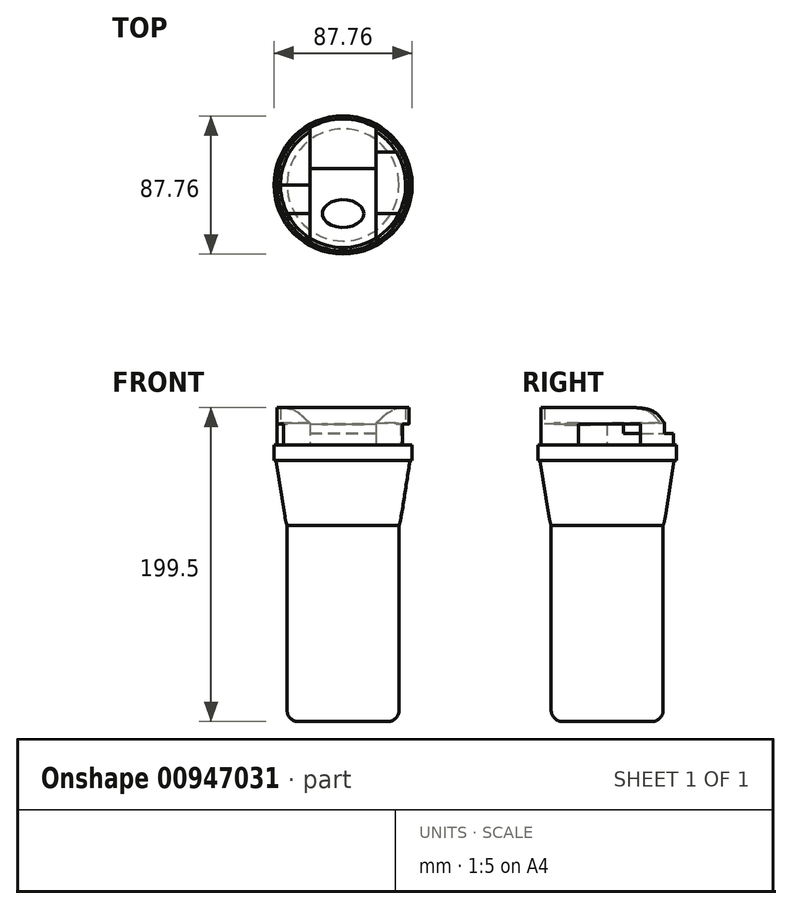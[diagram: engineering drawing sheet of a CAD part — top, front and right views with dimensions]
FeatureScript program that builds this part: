
annotation { "Feature Type Name" : "Feature", "Feature Type Description" : "" }
export const myFeature = defineFeature(function(context is Context, id is Id, definition is map)
    precondition{}
    {
        {
            var Q0;
            Q0=qCreatedBy(makeId("Top.planeOp"),FACE);
            var sketch = newSketch(context, id + "F0", { "sketchPlane" : qUnion([Q0])});
            skCircle(sketch, "E0", {"center": v(0, 0) * mm, "radius": 35.56 * mm});
            skSolve(sketch);
        }
        {
            var Q0;
            Q0 = qSketchRegion(id + "F0", true);
            extrude(context, id + "F1", {"entities" : qUnion([Q0]), "depth" : 124.6 * mm, "offsetDistance" : 25 * mm});
        }
        {
            var Q0;
            Q0=makeQuery(id+"F1.opExtrude","CAP_FACE",FACE,{"disambiguationData":[OSD([sQuery(id+"F0.wireOp",EDGE,"E0")])],"isStart":false});
            var sketch = newSketch(context, id + "F2", { "sketchPlane" : qUnion([Q0])});
            skCircle(sketch, "E1", {"center": v(0, 0) * mm, "radius": 36.06 * mm});
            skSolve(sketch);
        }
        {
            var Q0;
            Q0 = qSketchRegion(id + "F2", true);
            extrude(context, id + "F3", {"entities" : qUnion([Q0]), "operationType" : NewBodyOperationType.ADD, "depth" : 41.22 * mm, "offsetDistance" : 25 * mm});
        }
        {
            var Q0;
            Q0=makeQuery(id+"F3.opExtrude","CAP_FACE",FACE,{"disambiguationData":[OSD([sQuery(id+"F2.wireOp",EDGE,"E1")])],"isStart":false});
            var sketch = newSketch(context, id + "F4", { "sketchPlane" : qUnion([Q0])});
            skCircle(sketch, "E2", {"center": v(0, 0) * mm, "radius": 42.57 * mm});
            skSolve(sketch);
        }
        {
            var Q0;
            Q0 = qSketchRegion(id + "F4", true);
            extrude(context, id + "F5", {"entities" : qUnion([Q0]), "operationType" : NewBodyOperationType.ADD, "depth" : 0.1 * mm, "offsetDistance" : 25 * mm});
        }
        {
            var Q1;
            Q1 = qSketchRegion(id + "F4", true);
            var Q2;
            Q2 = qSketchRegion(id + "F2", true);
            loft(context, id + "F6", {"operationType" : NewBodyOperationType.ADD, "sheetProfilesArray" : [{ "sheetProfileEntities" : qUnion([Q1]) }, { "sheetProfileEntities" : qUnion([Q2]) }]});
        }
        {
            var Q0;
            Q0=makeQuery(id+"F5.opExtrude","CAP_FACE",FACE,{"disambiguationData":[OSD([sQuery(id+"F4.wireOp",EDGE,"E2")])],"isStart":false});
            var sketch = newSketch(context, id + "F7", { "sketchPlane" : qUnion([Q0])});
            skCircle(sketch, "E3", {"center": v(0, 0) * mm, "radius": 43.88 * mm});
            skSolve(sketch);
        }
        {
            var Q0;
            Q0 = qSketchRegion(id + "F7", true);
            extrude(context, id + "F8", {"entities" : qUnion([Q0]), "operationType" : NewBodyOperationType.ADD, "depth" : 9.9 * mm, "offsetDistance" : 25 * mm});
        }
        {
            var Q0;
            Q0=makeQuery(id+"F8.opExtrude","CAP_FACE",FACE,{"disambiguationData":[OSD([sQuery(id+"F7.wireOp",EDGE,"E3")])],"isStart":false});
            var sketch = newSketch(context, id + "F9", { "sketchPlane" : qUnion([Q0])});
            skCircle(sketch, "E4", {"center": v(0, 0) * mm, "radius": 41.98 * mm});
            skLineSegment(sketch, "E5", {"start": v(-41.98, 0) * mm, "end": v(41.98, 0) * mm});
            skLineSegment(sketch, "E6", {"start": v(0, 43.88) * mm, "end": v(0, -43.88) * mm});
            skLineSegment(sketch, "E7", {"start": v(0, 0) * mm, "end": v(41.98, 0) * mm});
            skLineSegment(sketch, "E8", {"start": v(0, 0) * mm, "end": v(-41.98, 0) * mm});
            skLineSegment(sketch, "E9", {"start": v(-20.99, 0) * mm, "end": v(-20.99, 36.35) * mm});
            skLineSegment(sketch, "E10", {"start": v(-20.99, 0) * mm, "end": v(-20.99, -36.35) * mm});
            skLineSegment(sketch, "E11", {"start": v(20.99, 0) * mm, "end": v(20.99, 36.35) * mm});
            skLineSegment(sketch, "E12", {"start": v(20.99, 0) * mm, "end": v(20.99, -36.35) * mm});
            skLineSegment(sketch, "E13", {"start": v(0, 0) * mm, "end": v(0, -41.98) * mm});
            skLineSegment(sketch, "E14", {"start": v(0, 0) * mm, "end": v(0, 41.98) * mm});
            skLineSegment(sketch, "E15", {"start": v(0, 20.99) * mm, "end": v(-36.35, 20.99) * mm});
            skLineSegment(sketch, "E16", {"start": v(0, 20.99) * mm, "end": v(36.35, 20.99) * mm});
            skLineSegment(sketch, "E17", {"start": v(-37.84, -18.18) * mm, "end": v(0, -18.18) * mm});
            skPoint(sketch, "E17.startSnap0", {"position": v(-20.99, -18.18) * mm});
            skLineSegment(sketch, "E18", {"start": v(0, -18.18) * mm, "end": v(37.84, -18.18) * mm});
            skLineSegment(sketch, "E19", {"start": v(-20.99, 20.99) * mm, "end": v(-20.99, 0) * mm});
            skLineSegment(sketch, "E20", {"start": v(-20.99, 10.5) * mm, "end": v(20.99, 10.5) * mm});
            skEllipse(sketch, "E21", {"center": v(0, -18.18) * mm, "majorRadius": 13.21 * mm, "minorRadius": 8.8 * mm, "majorAxis": v(1, 0)});
            skSolve(sketch);
        }
        {
            var Q0;
            {var subQ0=sQuery(id+"F9.wireOp",EDGE,"E11");var subQ1=sQuery(id+"F9.wireOp",EDGE,"E4");var subQ2=makeQuery(id+"F9.imprint","INTERSECT",VERTEX,{"derivedFrom":[subQ1,subQ0]});Q0=makeQuery(id+"F9.imprint","IMPRINT",FACE,{"disambiguationData":[TD([[makeQuery(id+"F9.imprint","IMPRINT",EDGE,{"disambiguationData":[TD([[subQ2,1.0]])],"derivedFrom":subQ0}),1.0]])]});}
            var Q1;
            {var subQ0=sQuery(id+"F9.wireOp",EDGE,"E9");Q1=makeQuery(id+"F9.imprint","IMPRINT",FACE,{"disambiguationData":[TD([[makeQuery(id+"F9.imprint","IMPRINT",EDGE,{"derivedFrom":subQ0}),-1.0]])]});}
            var Q2;
            {var subQ3=sQuery(id+"F9.wireOp",EDGE,"E20");var subQ5=sQuery(id+"F9.wireOp",EDGE,"E19");var subQ7=makeQuery(id+"F9.imprint","INTERSECT",VERTEX,{"derivedFrom":[subQ5,subQ3]});Q2=makeQuery(id+"F9.imprint","IMPRINT",FACE,{"disambiguationData":[TD([[makeQuery(id+"F9.imprint","IMPRINT",EDGE,{"disambiguationData":[TD([[subQ7,-1.0]])],"derivedFrom":subQ3}),1.0]])]});}
            var Q3;
            {var subQ0=sQuery(id+"F9.wireOp",EDGE,"E20");var subQ1=sQuery(id+"F9.wireOp",EDGE,"E11");var subQ2=makeQuery(id+"F9.imprint","INTERSECT",VERTEX,{"derivedFrom":[subQ1,subQ0]});Q3=makeQuery(id+"F9.imprint","IMPRINT",FACE,{"disambiguationData":[TD([[makeQuery(id+"F9.imprint","IMPRINT",EDGE,{"disambiguationData":[TD([[subQ2,-1.0]])],"derivedFrom":subQ1}),1.0]])]});}
            extrude(context, id + "F10", {"entities" : qUnion([Q0, Q1, Q2, Q3]), "operationType" : NewBodyOperationType.ADD, "flatOperationType" : FlatOperationType.REMOVE, "depth" : 7.1 * mm, "offsetDistance" : 25 * mm, "domain" : OperationDomain.MODEL});
        }
        {
            var Q0;
            {var subQ0=sQuery(id+"F9.wireOp",EDGE,"E9");Q0=makeQuery(id+"F9.imprint","IMPRINT",FACE,{"disambiguationData":[TD([[makeQuery(id+"F9.imprint","IMPRINT",EDGE,{"derivedFrom":subQ0}),1.0]])]});}
            var Q1;
            {var subQ4=sQuery(id+"F9.wireOp",EDGE,"E8");var subQ5=sQuery(id+"F9.wireOp",EDGE,"E4");var subQ6=makeQuery(id+"F9.imprint","INTERSECT",VERTEX,{"derivedFrom":[subQ5,subQ4]});Q1=makeQuery(id+"F9.imprint","IMPRINT",FACE,{"disambiguationData":[TD([[makeQuery(id+"F9.imprint","IMPRINT",EDGE,{"disambiguationData":[TD([[subQ6,1.0]])],"derivedFrom":subQ5}),1.0]])]});}
            var Q2;
            {var subQ0=sQuery(id+"F9.wireOp",EDGE,"E8");var subQ1=sQuery(id+"F9.wireOp",EDGE,"E4");var subQ2=makeQuery(id+"F9.imprint","INTERSECT",VERTEX,{"derivedFrom":[subQ1,subQ0]});Q2=makeQuery(id+"F9.imprint","IMPRINT",FACE,{"disambiguationData":[TD([[makeQuery(id+"F9.imprint","IMPRINT",EDGE,{"disambiguationData":[TD([[subQ2,-1.0]])],"derivedFrom":subQ1}),1.0]])]});}
            var Q3;
            {var subQ0=sQuery(id+"F9.wireOp",EDGE,"E10");var subQ1=sQuery(id+"F9.wireOp",EDGE,"E4");var subQ2=makeQuery(id+"F9.imprint","INTERSECT",VERTEX,{"derivedFrom":[subQ1,subQ0]});Q3=makeQuery(id+"F9.imprint","IMPRINT",FACE,{"disambiguationData":[TD([[makeQuery(id+"F9.imprint","IMPRINT",EDGE,{"disambiguationData":[TD([[subQ2,1.0]])],"derivedFrom":subQ1}),1.0]])]});}
            var Q4;
            {var subQ0=sQuery(id+"F9.wireOp",EDGE,"E11");var subQ1=sQuery(id+"F9.wireOp",EDGE,"E4");var subQ2=makeQuery(id+"F9.imprint","INTERSECT",VERTEX,{"derivedFrom":[subQ1,subQ0]});Q4=makeQuery(id+"F9.imprint","IMPRINT",FACE,{"disambiguationData":[TD([[makeQuery(id+"F9.imprint","IMPRINT",EDGE,{"disambiguationData":[TD([[subQ2,1.0]])],"derivedFrom":subQ1}),1.0]])]});}
            var Q5;
            {var subQ4=sQuery(id+"F9.wireOp",EDGE,"E7");var subQ5=sQuery(id+"F9.wireOp",EDGE,"E4");var subQ6=makeQuery(id+"F9.imprint","INTERSECT",VERTEX,{"derivedFrom":[subQ5,subQ4]});Q5=makeQuery(id+"F9.imprint","IMPRINT",FACE,{"disambiguationData":[TD([[makeQuery(id+"F9.imprint","IMPRINT",EDGE,{"disambiguationData":[TD([[subQ6,-1.0]])],"derivedFrom":subQ5}),1.0]])]});}
            var Q6;
            {var subQ0=sQuery(id+"F9.wireOp",EDGE,"E7");var subQ1=sQuery(id+"F9.wireOp",EDGE,"E4");var subQ2=makeQuery(id+"F9.imprint","INTERSECT",VERTEX,{"derivedFrom":[subQ1,subQ0]});Q6=makeQuery(id+"F9.imprint","IMPRINT",FACE,{"disambiguationData":[TD([[makeQuery(id+"F9.imprint","IMPRINT",EDGE,{"disambiguationData":[TD([[subQ2,1.0]])],"derivedFrom":subQ1}),1.0]])]});}
            var Q7;
            {var subQ0=sQuery(id+"F9.wireOp",EDGE,"E12");var subQ1=sQuery(id+"F9.wireOp",EDGE,"E4");var subQ2=makeQuery(id+"F9.imprint","INTERSECT",VERTEX,{"derivedFrom":[subQ1,subQ0]});Q7=makeQuery(id+"F9.imprint","IMPRINT",FACE,{"disambiguationData":[TD([[makeQuery(id+"F9.imprint","IMPRINT",EDGE,{"disambiguationData":[TD([[subQ2,-1.0]])],"derivedFrom":subQ1}),1.0]])]});}
            extrude(context, id + "F11", {"entities" : qUnion([Q0, Q1, Q2, Q3, Q4, Q5, Q6, Q7]), "operationType" : NewBodyOperationType.ADD, "flatOperationType" : FlatOperationType.REMOVE, "depth" : 14 * mm, "offsetDistance" : 25 * mm, "domain" : OperationDomain.MODEL});
        }
        {
            var Q0;
            {var subQ3=sQuery(id+"F9.wireOp",EDGE,"E19");var subQ5=sQuery(id+"F9.wireOp",EDGE,"E20");var subQ6=makeQuery(id+"F9.imprint","INTERSECT",VERTEX,{"derivedFrom":[subQ3,subQ5]});Q0=makeQuery(id+"F9.imprint","IMPRINT",FACE,{"disambiguationData":[TD([[makeQuery(id+"F9.imprint","IMPRINT",EDGE,{"disambiguationData":[TD([[subQ6,-1.0]])],"derivedFrom":subQ5}),-1.0]])]});}
            var Q1;
            {var subQ3=sQuery(id+"F9.wireOp",EDGE,"E11");var subQ5=sQuery(id+"F9.wireOp",EDGE,"E20");var subQ6=makeQuery(id+"F9.imprint","INTERSECT",VERTEX,{"derivedFrom":[subQ3,subQ5]});Q1=makeQuery(id+"F9.imprint","IMPRINT",FACE,{"disambiguationData":[TD([[makeQuery(id+"F9.imprint","IMPRINT",EDGE,{"disambiguationData":[TD([[subQ6,1.0]])],"derivedFrom":subQ5}),-1.0]])]});}
            var Q2;
            {var subQ3=sQuery(id+"F9.wireOp",EDGE,"E12");var subQ5=sQuery(id+"F9.wireOp",EDGE,"E18");var subQ6=makeQuery(id+"F9.imprint","INTERSECT",VERTEX,{"derivedFrom":[subQ3,subQ5]});Q2=makeQuery(id+"F9.imprint","IMPRINT",FACE,{"disambiguationData":[TD([[makeQuery(id+"F9.imprint","IMPRINT",EDGE,{"disambiguationData":[TD([[subQ6,1.0]])],"derivedFrom":subQ3}),-1.0]])]});}
            var Q3;
            {var subQ3=sQuery(id+"F9.wireOp",EDGE,"E10");var subQ5=sQuery(id+"F9.wireOp",EDGE,"E17");var subQ7=makeQuery(id+"F9.imprint","INTERSECT",VERTEX,{"derivedFrom":[subQ3,subQ5]});Q3=makeQuery(id+"F9.imprint","IMPRINT",FACE,{"disambiguationData":[TD([[makeQuery(id+"F9.imprint","IMPRINT",EDGE,{"disambiguationData":[TD([[subQ7,1.0]])],"derivedFrom":subQ3}),1.0]])]});}
            var Q4;
            {var subQ0=sQuery(id+"F9.wireOp",EDGE,"E12");var subQ1=sQuery(id+"F9.wireOp",EDGE,"E4");var subQ2=makeQuery(id+"F9.imprint","INTERSECT",VERTEX,{"derivedFrom":[subQ1,subQ0]});Q4=makeQuery(id+"F9.imprint","IMPRINT",FACE,{"disambiguationData":[TD([[makeQuery(id+"F9.imprint","IMPRINT",EDGE,{"disambiguationData":[TD([[subQ2,1.0]])],"derivedFrom":subQ0}),-1.0]])]});}
            var Q5;
            {var subQ0=sQuery(id+"F9.wireOp",EDGE,"E10");var subQ1=sQuery(id+"F9.wireOp",EDGE,"E4");var subQ2=makeQuery(id+"F9.imprint","INTERSECT",VERTEX,{"derivedFrom":[subQ1,subQ0]});Q5=makeQuery(id+"F9.imprint","IMPRINT",FACE,{"disambiguationData":[TD([[makeQuery(id+"F9.imprint","IMPRINT",EDGE,{"disambiguationData":[TD([[subQ2,1.0]])],"derivedFrom":subQ0}),1.0]])]});}
            extrude(context, id + "F12", {"entities" : qUnion([Q0, Q1, Q2, Q3, Q4, Q5]), "operationType" : NewBodyOperationType.ADD, "flatOperationType" : FlatOperationType.REMOVE, "depth" : 13.4 * mm, "offsetDistance" : 25 * mm, "domain" : OperationDomain.MODEL});
        }
        {
            var Q0;
            {var subQ0=sQuery(id+"F2.wireOp",EDGE,"E1");Q0=makeQuery(id+"F6.boolean.opBoolean","MERGE",EDGE,{"derivedFrom":[makeQuery(id+"F3.opExtrude","CAP_EDGE",EDGE,{"disambiguationData":[OSD([subQ0])],"isStart":true}),makeQuery(id+"F6.opLoft","MID_CAP_EDGE",EDGE,{"disambiguationData":[OSD([subQ0])],"capPos":1.0})]});}
            fillet(context, id + "F13", {"entities" : qUnion([Q0]), "radius" : 34.87 * mm, "tangentPropagation" : true, "allowEdgeOverflow" : false});
        }
        {
            var Q0;
            Q0=makeQuery(id+"F1.opExtrude","CAP_EDGE",EDGE,{"disambiguationData":[OSD([sQuery(id+"F0.wireOp",EDGE,"E0")])],"isStart":true});
            fillet(context, id + "F14", {"entities" : qUnion([Q0]), "radius" : 7.24 * mm, "tangentPropagation" : true, "allowEdgeOverflow" : false});
        }
        {
            var Q0;
            {var subQ1=sQuery(id+"F9.wireOp",EDGE,"E13");var subQ3=sQuery(id+"F9.wireOp",EDGE,"E21");var subQ4=makeQuery(id+"F9.imprint","INTERSECT",VERTEX,{"disambiguationData":[OD(0.0)],"derivedFrom":[subQ1,subQ3]});Q0=makeQuery(id+"F9.imprint","IMPRINT",FACE,{"disambiguationData":[TD([[makeQuery(id+"F9.imprint","IMPRINT",EDGE,{"disambiguationData":[TD([[subQ4,-1.0]])],"derivedFrom":subQ3}),1.0]])]});}
            var Q1;
            {var subQ1=sQuery(id+"F9.wireOp",EDGE,"E13");var subQ3=sQuery(id+"F9.wireOp",EDGE,"E21");var subQ4=makeQuery(id+"F9.imprint","INTERSECT",VERTEX,{"disambiguationData":[OD(0.0)],"derivedFrom":[subQ1,subQ3]});Q1=makeQuery(id+"F9.imprint","IMPRINT",FACE,{"disambiguationData":[TD([[makeQuery(id+"F9.imprint","IMPRINT",EDGE,{"disambiguationData":[TD([[subQ4,1.0]])],"derivedFrom":subQ3}),1.0]])]});}
            var Q2;
            {var subQ1=sQuery(id+"F9.wireOp",EDGE,"E13");var subQ3=sQuery(id+"F9.wireOp",EDGE,"E21");var subQ4=makeQuery(id+"F9.imprint","INTERSECT",VERTEX,{"disambiguationData":[OD(1.0)],"derivedFrom":[subQ1,subQ3]});Q2=makeQuery(id+"F9.imprint","IMPRINT",FACE,{"disambiguationData":[TD([[makeQuery(id+"F9.imprint","IMPRINT",EDGE,{"disambiguationData":[TD([[subQ4,-1.0]])],"derivedFrom":subQ3}),1.0]])]});}
            var Q3;
            {var subQ1=sQuery(id+"F9.wireOp",EDGE,"E13");var subQ3=sQuery(id+"F9.wireOp",EDGE,"E21");var subQ4=makeQuery(id+"F9.imprint","INTERSECT",VERTEX,{"disambiguationData":[OD(1.0)],"derivedFrom":[subQ1,subQ3]});Q3=makeQuery(id+"F9.imprint","IMPRINT",FACE,{"disambiguationData":[TD([[makeQuery(id+"F9.imprint","IMPRINT",EDGE,{"disambiguationData":[TD([[subQ4,1.0]])],"derivedFrom":subQ3}),1.0]])]});}
            extrude(context, id + "F15", {"entities" : qUnion([Q0, Q1, Q2, Q3]), "operationType" : NewBodyOperationType.ADD, "flatOperationType" : FlatOperationType.REMOVE, "depth" : 12.5 * mm, "offsetDistance" : 25 * mm, "domain" : OperationDomain.MODEL});
        }
        {
            var Q0;
            Q0=makeQuery(id+"F12.opExtrude","CAP_FACE",FACE,{"disambiguationData":[OSD([sQuery(id+"F9.wireOp",EDGE,"E4"),sQuery(id+"F9.wireOp",EDGE,"E10"),sQuery(id+"F9.wireOp",EDGE,"E11"),sQuery(id+"F9.wireOp",EDGE,"E12"),sQuery(id+"F9.wireOp",EDGE,"E19"),sQuery(id+"F9.wireOp",EDGE,"E20"),sQuery(id+"F9.wireOp",EDGE,"E21")])],"isStart":false});
            var sketch = newSketch(context, id + "F16", { "sketchPlane" : qUnion([Q0])});
            skCircle(sketch, "E22", {"center": v(0, 0) * mm, "radius": 41.98 * mm});
            skLineSegment(sketch, "E23", {"start": v(-21.34, 36.15) * mm, "end": v(21.34, 36.15) * mm});
            skLineSegment(sketch, "E24", {"start": v(21.34, 36.15) * mm, "end": v(20.99, 10.5) * mm});
            skLineSegment(sketch, "E25", {"start": v(20.99, 10.5) * mm, "end": v(-20.99, 10.5) * mm});
            skLineSegment(sketch, "E26", {"start": v(-20.99, 10.5) * mm, "end": v(-21.34, 36.15) * mm});
            skCircle(sketch, "E27", {"center": v(0, 0) * mm, "radius": 39.74 * mm});
            skSolve(sketch);
        }
        {
            var Q0;
            {var subQ3=sQuery(id+"F16.wireOp",EDGE,"E26");var subQ5=sQuery(id+"F16.wireOp",EDGE,"E27");var subQ6=makeQuery(id+"F16.imprint","INTERSECT",VERTEX,{"derivedFrom":[subQ3,subQ5]});Q0=makeQuery(id+"F16.imprint","IMPRINT",FACE,{"disambiguationData":[TD([[makeQuery(id+"F16.imprint","IMPRINT",EDGE,{"disambiguationData":[TD([[subQ6,-1.0]])],"derivedFrom":subQ3}),1.0]])]});}
            var Q1;
            {var subQ3=sQuery(id+"F16.wireOp",EDGE,"E24");var subQ5=sQuery(id+"F16.wireOp",EDGE,"E27");var subQ6=makeQuery(id+"F16.imprint","INTERSECT",VERTEX,{"derivedFrom":[subQ3,subQ5]});Q1=makeQuery(id+"F16.imprint","IMPRINT",FACE,{"disambiguationData":[TD([[makeQuery(id+"F16.imprint","IMPRINT",EDGE,{"disambiguationData":[TD([[subQ6,1.0]])],"derivedFrom":subQ3}),1.0]])]});}
            var Q2;
            {var subQ0=sQuery(id+"F16.wireOp",EDGE,"E22");var subQ1=makeQuery(id+"F12.opExtrude","CAP_EDGE",EDGE,{"disambiguationData":[OSD([sQuery(id+"F9.wireOp",EDGE,"E10"),sQuery(id+"F9.wireOp",EDGE,"E19")])],"isStart":false});var subQ2=makeQuery(id+"F16.imprint","INTERSECT",VERTEX,{"derivedFrom":[subQ1,subQ0]});Q2=makeQuery(id+"F16.imprint","IMPRINT",FACE,{"disambiguationData":[TD([[makeQuery(id+"F16.imprint","IMPRINT",EDGE,{"disambiguationData":[TD([[subQ2,-1.0]])],"derivedFrom":subQ0}),1.0]])]});}
            extrude(context, id + "F17", {"entities" : qUnion([Q0, Q1, Q2]), "operationType" : NewBodyOperationType.ADD, "depth" : 10.3 * mm, "offsetDistance" : 25 * mm});
        }
        {
            var Q0;
            Q0=makeQuery(id+"F17.opExtrude","CAP_EDGE",EDGE,{"disambiguationData":[OSD([sQuery(id+"F16.wireOp",EDGE,"E24")])],"isStart":false});
            var Q1;
            Q1=makeQuery(id+"F17.opExtrude","CAP_EDGE",EDGE,{"disambiguationData":[OSD([sQuery(id+"F16.wireOp",EDGE,"E26")])],"isStart":false});
            chamfer(context, id + "F18", {"entities" : qUnion([Q0, Q1]), "width" : 10 * mm, "tangentPropagation" : true});
        }
        {
            var Q0;
            Q0=makeQuery(id+"F12.opExtrude","CAP_EDGE",EDGE,{"disambiguationData":[OSD([sQuery(id+"F9.wireOp",EDGE,"E20")])],"isStart":false});
            fillet(context, id + "F19", {"entities" : qUnion([Q0]), "radius" : 2 * mm, "tangentPropagation" : true, "allowEdgeOverflow" : false});
        }
        {
            var Q0;
            {var subQ0=sQuery(id+"F4.wireOp",EDGE,"E2");Q0=makeQuery(id+"F6.boolean.opBoolean","MERGE",EDGE,{"derivedFrom":[makeQuery(id+"F5.opExtrude","CAP_EDGE",EDGE,{"disambiguationData":[OSD([subQ0])],"isStart":true}),makeQuery(id+"F6.opLoft","MID_CAP_EDGE",EDGE,{"disambiguationData":[OSD([subQ0])],"capPos":0.0})]});}
            fillet(context, id + "F20", {"entities" : qUnion([Q0]), "radius" : 3.26 * mm, "tangentPropagation" : true, "allowEdgeOverflow" : false});
        }
        {
            var Q0;
            Q0=makeQuery(id+"F18.opChamfer","BLEND_EDGE",EDGE,{"blendedFrom":[makeQuery(id+"F17.opExtrude","CAP_EDGE",EDGE,{"disambiguationData":[OSD([sQuery(id+"F16.wireOp",EDGE,"E26")])],"isStart":false}),makeQuery(id+"F11.opExtrude","CAP_FACE",FACE,{"disambiguationData":[OSD([sQuery(id+"F9.wireOp",EDGE,"E4"),sQuery(id+"F9.wireOp",EDGE,"E9"),sQuery(id+"F9.wireOp",EDGE,"E10"),sQuery(id+"F9.wireOp",EDGE,"E19")])],"isStart":false})],"blendedInto":[makeQuery(id+"F11.opExtrude","CAP_FACE",FACE,{"disambiguationData":[OSD([sQuery(id+"F9.wireOp",EDGE,"E4"),sQuery(id+"F9.wireOp",EDGE,"E9"),sQuery(id+"F9.wireOp",EDGE,"E10"),sQuery(id+"F9.wireOp",EDGE,"E19")])],"isStart":false})]});
            var Q1;
            {var subQ0=sQuery(id+"F16.wireOp",EDGE,"E26");Q1=makeQuery(id+"F18.opChamfer","BLEND_EDGE",EDGE,{"blendedFrom":[makeQuery(id+"F17.opExtrude","CAP_EDGE",EDGE,{"disambiguationData":[OSD([subQ0])],"isStart":false}),makeQuery(id+"F17.opExtrude","CAP_FACE",FACE,{"disambiguationData":[OSD([sQuery(id+"F16.wireOp",EDGE,"E22"),sQuery(id+"F16.wireOp",EDGE,"E24"),subQ0,sQuery(id+"F16.wireOp",EDGE,"E27")])],"isStart":false})],"blendedInto":[makeQuery(id+"F17.opExtrude","CAP_FACE",FACE,{"disambiguationData":[OSD([sQuery(id+"F16.wireOp",EDGE,"E22"),sQuery(id+"F16.wireOp",EDGE,"E24"),subQ0,sQuery(id+"F16.wireOp",EDGE,"E27")])],"isStart":false})]});}
            var Q2;
            Q2=makeQuery(id+"F18.opChamfer","BLEND_EDGE",EDGE,{"blendedFrom":[makeQuery(id+"F17.opExtrude","CAP_EDGE",EDGE,{"disambiguationData":[OSD([sQuery(id+"F16.wireOp",EDGE,"E24")])],"isStart":false}),makeQuery(id+"F11.opExtrude","CAP_FACE",FACE,{"disambiguationData":[OSD([sQuery(id+"F9.wireOp",EDGE,"E4"),sQuery(id+"F9.wireOp",EDGE,"E11"),sQuery(id+"F9.wireOp",EDGE,"E12")])],"isStart":false})],"blendedInto":[makeQuery(id+"F11.opExtrude","CAP_FACE",FACE,{"disambiguationData":[OSD([sQuery(id+"F9.wireOp",EDGE,"E4"),sQuery(id+"F9.wireOp",EDGE,"E11"),sQuery(id+"F9.wireOp",EDGE,"E12")])],"isStart":false})]});
            var Q3;
            {var subQ0=sQuery(id+"F16.wireOp",EDGE,"E24");Q3=makeQuery(id+"F18.opChamfer","BLEND_EDGE",EDGE,{"blendedFrom":[makeQuery(id+"F17.opExtrude","CAP_EDGE",EDGE,{"disambiguationData":[OSD([subQ0])],"isStart":false}),makeQuery(id+"F17.opExtrude","CAP_FACE",FACE,{"disambiguationData":[OSD([sQuery(id+"F16.wireOp",EDGE,"E22"),subQ0,sQuery(id+"F16.wireOp",EDGE,"E26"),sQuery(id+"F16.wireOp",EDGE,"E27")])],"isStart":false})],"blendedInto":[makeQuery(id+"F17.opExtrude","CAP_FACE",FACE,{"disambiguationData":[OSD([sQuery(id+"F16.wireOp",EDGE,"E22"),subQ0,sQuery(id+"F16.wireOp",EDGE,"E26"),sQuery(id+"F16.wireOp",EDGE,"E27")])],"isStart":false})]});}
            fillet(context, id + "F21", {"entities" : qUnion([Q0, Q1, Q2, Q3]), "radius" : 20.63 * mm, "tangentPropagation" : true, "allowEdgeOverflow" : false});
        }
    });
